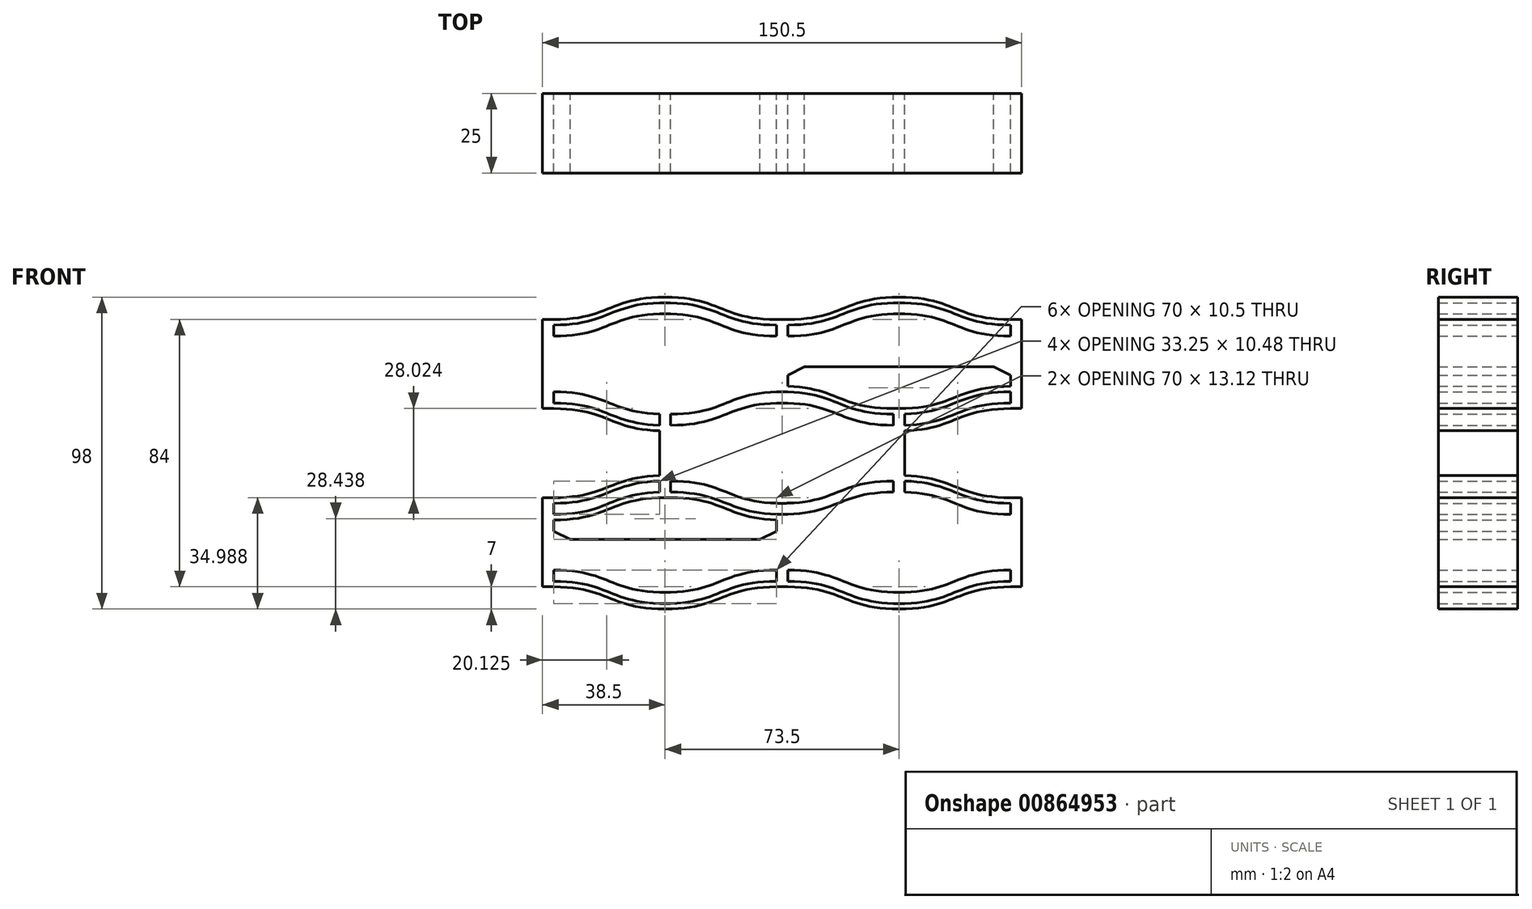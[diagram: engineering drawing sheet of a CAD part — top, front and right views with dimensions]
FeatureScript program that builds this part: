
annotation { "Feature Type Name" : "Feature", "Feature Type Description" : "" }
export const myFeature = defineFeature(function(context is Context, id is Id, definition is map)
    precondition{}
    {
        {
            var Q0;
            Q0=qCreatedBy(makeId("Front.planeOp"),FACE);
            var sketch = newSketch(context, id + "F0", { "sketchPlane" : qUnion([Q0])});
            skPoint(sketch, "E0", {"position": v(0, 0) * mm});
            skFitSpline(sketch, "E1", {"points": [v(38.5, -7) * mm, v(56, -3.5) * mm, v(73.5, 0) * mm], "startDerivative": vector(52.5, 0) * mm, "endDerivative": vector(52.5, 0) * mm});
            skFitSpline(sketch, "E2", {"points": [v(73.5, 7) * mm, v(56, 3.5) * mm, v(38.5, 0) * mm], "startDerivative": vector(-52.5, 0) * mm, "endDerivative": vector(-52.5, 0) * mm});
            skFitSpline(sketch, "E3", {"points": [v(73.5, 5.25) * mm, v(56, 1.75) * mm, v(38.5, -1.75) * mm], "startDerivative": vector(-52.5, 0) * mm, "endDerivative": vector(-52.5, 0) * mm});
            skFitSpline(sketch, "E4", {"points": [v(73.5, 1.75) * mm, v(56, -1.75) * mm, v(38.5, -5.25) * mm], "startDerivative": vector(-52.5, 0) * mm, "endDerivative": vector(-52.5, 0) * mm});
            skLineSegment(sketch, "E5", {"start": v(73.5, 26.25) * mm, "end": v(73.5, 22.75) * mm});
            skLineSegment(sketch, "E6", {"start": v(70, 0) * mm, "end": v(73.5, 0) * mm});
            skLineSegment(sketch, "E7.trimOffspring", {"start": v(73.5, 5.25) * mm, "end": v(73.5, 1.75) * mm});
            skLineSegment(sketch, "E8.trimOffspring", {"start": v(73.5, 10.5) * mm, "end": v(73.5, 7) * mm});
            skLineSegment(sketch, "E9.trimOffspring", {"start": v(73.5, 21) * mm, "end": v(73.5, 17.5) * mm});
            skLineSegment(sketch, "E10", {"start": v(73.5, 1.75) * mm, "end": v(73.5, 5.25) * mm});
            skLineSegment(sketch, "E11", {"start": v(3.5, 26.25) * mm, "end": v(3.5, 22.75) * mm});
            skLineSegment(sketch, "E12", {"start": v(68.25, 13.13) * mm, "end": v(8.75, 13.13) * mm});
            skLineSegment(sketch, "E13", {"start": v(68.25, 14.88) * mm, "end": v(8.75, 14.88) * mm});
            skLineSegment(sketch, "E14", {"start": v(3.5, 28) * mm, "end": v(0, 28) * mm});
            skLineSegment(sketch, "E15", {"start": v(73.5, 17.5) * mm, "end": v(68.25, 14.87) * mm});
            skLineSegment(sketch, "E16", {"start": v(68.25, 13.13) * mm, "end": v(73.5, 10.5) * mm});
            skLineSegment(sketch, "E17", {"start": v(3.5, 10.5) * mm, "end": v(8.75, 13.12) * mm});
            skLineSegment(sketch, "E18", {"start": v(3.5, 17.5) * mm, "end": v(8.75, 14.87) * mm});
            skFitSpline(sketch, "E19", {"points": [v(73.5, 21) * mm, v(56, 24.5) * mm, v(38.5, 28) * mm], "startDerivative": vector(-52.5, 0) * mm, "endDerivative": vector(-52.5, 0) * mm});
            skFitSpline(sketch, "E20", {"points": [v(73.5, 22.75) * mm, v(56, 26.25) * mm, v(38.5, 29.75) * mm], "startDerivative": vector(-52.5, 0) * mm, "endDerivative": vector(-52.5, 0) * mm});
            skFitSpline(sketch, "E21", {"points": [v(73.5, 26.25) * mm, v(56, 29.75) * mm, v(38.5, 33.25) * mm], "startDerivative": vector(-52.5, 0) * mm, "endDerivative": vector(-52.5, 0) * mm});
            skFitSpline(sketch, "E22", {"points": [v(73.5, 28) * mm, v(56, 31.5) * mm, v(38.5, 35) * mm], "startDerivative": vector(-52.5, 0) * mm, "endDerivative": vector(-52.5, 0) * mm});
            skFitSpline(sketch, "E23", {"points": [v(3.5, 1.75) * mm, v(21, -1.75) * mm, v(38.5, -5.25) * mm], "startDerivative": vector(52.5, 0) * mm, "endDerivative": vector(52.5, 0) * mm});
            skFitSpline(sketch, "E24", {"points": [v(3.5, 0) * mm, v(21, -3.5) * mm, v(38.5, -7) * mm], "startDerivative": vector(52.5, 0) * mm, "endDerivative": vector(52.5, 0) * mm});
            skFitSpline(sketch, "E25", {"points": [v(38.5, -1.75) * mm, v(21, 1.75) * mm, v(3.5, 5.25) * mm], "startDerivative": vector(-52.5, 0) * mm, "endDerivative": vector(-52.5, 0) * mm});
            skFitSpline(sketch, "E26", {"points": [v(38.5, 0) * mm, v(21, 3.5) * mm, v(3.5, 6.97) * mm], "startDerivative": vector(-52.5, 0) * mm, "endDerivative": vector(-52.5, 0) * mm});
            skFitSpline(sketch, "E27", {"points": [v(73.5, 7) * mm, v(56, 3.5) * mm, v(38.5, 0) * mm], "startDerivative": vector(-52.5, 0) * mm, "endDerivative": vector(-52.5, 0) * mm});
            skFitSpline(sketch, "E28", {"points": [v(38.5, 35) * mm, v(21, 31.5) * mm, v(3.5, 28) * mm], "startDerivative": vector(-52.5, 0) * mm, "endDerivative": vector(-52.5, 0) * mm});
            skFitSpline(sketch, "E29", {"points": [v(38.5, 33.25) * mm, v(21, 29.75) * mm, v(3.5, 26.25) * mm], "startDerivative": vector(-52.5, 0) * mm, "endDerivative": vector(-52.5, 0) * mm});
            skFitSpline(sketch, "E30", {"points": [v(38.5, 29.75) * mm, v(21, 26.25) * mm, v(3.5, 22.75) * mm], "startDerivative": vector(-52.5, 0) * mm, "endDerivative": vector(-52.5, 0) * mm});
            skFitSpline(sketch, "E31", {"points": [v(38.5, 27.97) * mm, v(21, 24.47) * mm, v(3.5, 20.97) * mm], "startDerivative": vector(-52.5, 0) * mm, "endDerivative": vector(-52.5, 0) * mm});
            skFitSpline(sketch, "E32", {"points": [v(38.5, -7) * mm, v(56, -3.5) * mm, v(73.5, 0) * mm], "startDerivative": vector(52.5, 0) * mm, "endDerivative": vector(52.5, 0) * mm});
            skFitSpline(sketch, "E33", {"points": [v(38.5, -5.25) * mm, v(56, -1.75) * mm, v(73.5, 1.75) * mm], "startDerivative": vector(52.5, 0) * mm, "endDerivative": vector(52.5, 0) * mm});
            skFitSpline(sketch, "E34", {"points": [v(38.5, -1.75) * mm, v(56, 1.75) * mm, v(73.5, 5.25) * mm], "startDerivative": vector(52.5, 0) * mm, "endDerivative": vector(52.5, 0) * mm});
            skLineSegment(sketch, "E35", {"start": v(40.25, -3.53) * mm, "end": v(40.25, -5.23) * mm});
            skLineSegment(sketch, "E36", {"start": v(40.25, -5.23) * mm, "end": v(40.25, -1.73) * mm});
            skLineSegment(sketch, "E37", {"start": v(36.75, -3.53) * mm, "end": v(36.75, -5.23) * mm});
            skLineSegment(sketch, "E38", {"start": v(36.75, -5.23) * mm, "end": v(36.75, -1.73) * mm});
            skLineSegment(sketch, "E39", {"start": v(40.25, 31.53) * mm, "end": v(40.25, 29.73) * mm});
            skLineSegment(sketch, "E40", {"start": v(40.25, 29.73) * mm, "end": v(40.25, 33.23) * mm});
            skLineSegment(sketch, "E41", {"start": v(36.75, 29.73) * mm, "end": v(36.75, 33.23) * mm});
            skLineSegment(sketch, "E42.trimOffspring", {"start": v(73.5, 22.75) * mm, "end": v(73.5, 26.25) * mm});
            skLineSegment(sketch, "E43.trimOffspring", {"start": v(73.5, 17.5) * mm, "end": v(73.5, 21) * mm});
            skLineSegment(sketch, "E44.trimOffspring", {"start": v(73.5, 7) * mm, "end": v(73.5, 10.5) * mm});
            skLineSegment(sketch, "E45.trimOffspring", {"start": v(3.5, 21) * mm, "end": v(3.5, 17.5) * mm});
            skLineSegment(sketch, "E46.trimOffspring", {"start": v(3.5, 10.5) * mm, "end": v(3.5, 7) * mm});
            skLineSegment(sketch, "E47.trimOffspring", {"start": v(3.5, 5.25) * mm, "end": v(3.5, 1.75) * mm});
            skLineSegment(sketch, "E48.left", {"start": v(0, 26.27) * mm, "end": v(0, 22.77) * mm});
            skPoint(sketch, "E49", {"position": v(77, 28) * mm});
            skLineSegment(sketch, "E50", {"start": v(75.25, 28) * mm, "end": v(76.25, 28) * mm});
            skLineSegment(sketch, "E51", {"start": v(77, 1.73) * mm, "end": v(77, 21.02) * mm});
            skLineSegment(sketch, "E52", {"start": v(73.5, 0) * mm, "end": v(77, 0) * mm});
            skPoint(sketch, "E53", {"position": v(36.75, 28) * mm});
            skLineSegment(sketch, "E54", {"start": v(76.25, 28) * mm, "end": v(75.25, 28) * mm});
            skLineSegment(sketch, "E55", {"start": v(71.75, 28) * mm, "end": v(75.25, 28) * mm});
            skFitSpline(sketch, "E56", {"points": [v(75.25, 21) * mm, v(92.75, 24.5) * mm, v(110.25, 28) * mm], "startDerivative": vector(52.5, 0) * mm, "endDerivative": vector(52.5, 0) * mm});
            skFitSpline(sketch, "E57", {"points": [v(110.25, 35) * mm, v(92.75, 31.5) * mm, v(75.25, 28) * mm], "startDerivative": vector(-52.5, 0) * mm, "endDerivative": vector(-52.5, 0) * mm});
            skFitSpline(sketch, "E58", {"points": [v(110.25, 33.25) * mm, v(92.75, 29.75) * mm, v(75.25, 26.25) * mm], "startDerivative": vector(-52.5, 0) * mm, "endDerivative": vector(-52.5, 0) * mm});
            skFitSpline(sketch, "E59", {"points": [v(110.25, 29.75) * mm, v(92.75, 26.25) * mm, v(75.25, 22.75) * mm], "startDerivative": vector(-52.5, 0) * mm, "endDerivative": vector(-52.5, 0) * mm});
            skLineSegment(sketch, "E60", {"start": v(110.25, 56) * mm, "end": v(106.75, 56) * mm});
            skLineSegment(sketch, "E61", {"start": v(106.75, 56) * mm, "end": v(110.25, 56) * mm});
            skLineSegment(sketch, "E62", {"start": v(110.25, 54.25) * mm, "end": v(110.25, 50.75) * mm});
            skLineSegment(sketch, "E63", {"start": v(106.75, 28) * mm, "end": v(110.25, 28) * mm});
            skLineSegment(sketch, "E64.trimOffspring", {"start": v(110.25, 33.25) * mm, "end": v(110.25, 29.75) * mm});
            skLineSegment(sketch, "E65.trimOffspring", {"start": v(110.25, 38.5) * mm, "end": v(110.25, 35) * mm});
            skLineSegment(sketch, "E66.trimOffspring", {"start": v(110.25, 49) * mm, "end": v(110.25, 45.5) * mm});
            skLineSegment(sketch, "E67", {"start": v(110.25, 29.75) * mm, "end": v(110.25, 33.25) * mm});
            skLineSegment(sketch, "E68", {"start": v(36.75, 29.73) * mm, "end": v(36.75, 33.25) * mm});
            skLineSegment(sketch, "E69", {"start": v(40.25, 54.25) * mm, "end": v(40.25, 50.75) * mm});
            skLineSegment(sketch, "E70", {"start": v(105, 41.12) * mm, "end": v(45.5, 41.13) * mm});
            skLineSegment(sketch, "E71", {"start": v(105, 42.87) * mm, "end": v(45.5, 42.88) * mm});
            skLineSegment(sketch, "E72", {"start": v(110.25, 45.5) * mm, "end": v(105, 42.87) * mm});
            skLineSegment(sketch, "E73", {"start": v(105, 41.13) * mm, "end": v(110.25, 38.5) * mm});
            skLineSegment(sketch, "E74", {"start": v(40.25, 38.5) * mm, "end": v(45.5, 41.12) * mm});
            skLineSegment(sketch, "E75", {"start": v(40.25, 45.5) * mm, "end": v(45.5, 42.88) * mm});
            skFitSpline(sketch, "E76", {"points": [v(110.25, 49) * mm, v(92.75, 52.5) * mm, v(75.25, 56) * mm], "startDerivative": vector(-52.5, 0) * mm, "endDerivative": vector(-52.5, 0) * mm});
            skFitSpline(sketch, "E77", {"points": [v(110.25, 50.75) * mm, v(92.75, 54.25) * mm, v(75.25, 57.75) * mm], "startDerivative": vector(-52.5, 0) * mm, "endDerivative": vector(-52.5, 0) * mm});
            skFitSpline(sketch, "E78", {"points": [v(110.25, 54.25) * mm, v(92.75, 57.75) * mm, v(75.25, 61.25) * mm], "startDerivative": vector(-52.5, 0) * mm, "endDerivative": vector(-52.5, 0) * mm});
            skFitSpline(sketch, "E79", {"points": [v(110.25, 56) * mm, v(92.75, 59.5) * mm, v(75.25, 63) * mm], "startDerivative": vector(-52.5, 0) * mm, "endDerivative": vector(-52.5, 0) * mm});
            skFitSpline(sketch, "E80", {"points": [v(110.25, 35) * mm, v(92.75, 31.5) * mm, v(75.25, 28) * mm], "startDerivative": vector(-52.5, 0) * mm, "endDerivative": vector(-52.5, 0) * mm});
            skFitSpline(sketch, "E81", {"points": [v(75.25, 63) * mm, v(57.75, 59.5) * mm, v(40.25, 56) * mm], "startDerivative": vector(-52.5, 0) * mm, "endDerivative": vector(-52.5, 0) * mm});
            skFitSpline(sketch, "E82", {"points": [v(75.25, 61.25) * mm, v(57.75, 57.75) * mm, v(40.25, 54.25) * mm], "startDerivative": vector(-52.5, 0) * mm, "endDerivative": vector(-52.5, 0) * mm});
            skFitSpline(sketch, "E83", {"points": [v(75.25, 57.75) * mm, v(57.75, 54.25) * mm, v(40.25, 50.75) * mm], "startDerivative": vector(-52.5, 0) * mm, "endDerivative": vector(-52.5, 0) * mm});
            skFitSpline(sketch, "E84", {"points": [v(75.25, 55.97) * mm, v(57.75, 52.47) * mm, v(40.25, 48.97) * mm], "startDerivative": vector(-52.5, 0) * mm, "endDerivative": vector(-52.5, 0) * mm});
            skFitSpline(sketch, "E85", {"points": [v(75.25, 21) * mm, v(92.75, 24.5) * mm, v(110.25, 28) * mm], "startDerivative": vector(52.5, 0) * mm, "endDerivative": vector(52.5, 0) * mm});
            skFitSpline(sketch, "E86", {"points": [v(75.25, 22.75) * mm, v(92.75, 26.25) * mm, v(110.25, 29.75) * mm], "startDerivative": vector(52.5, 0) * mm, "endDerivative": vector(52.5, 0) * mm});
            skFitSpline(sketch, "E87", {"points": [v(75.25, 26.25) * mm, v(92.75, 29.75) * mm, v(110.25, 33.25) * mm], "startDerivative": vector(52.5, 0) * mm, "endDerivative": vector(52.5, 0) * mm});
            skLineSegment(sketch, "E88", {"start": v(77, 24.47) * mm, "end": v(77, 22.77) * mm});
            skLineSegment(sketch, "E89", {"start": v(77, 22.77) * mm, "end": v(77, 26.27) * mm});
            skLineSegment(sketch, "E90", {"start": v(73.5, 24.47) * mm, "end": v(73.5, 22.77) * mm});
            skLineSegment(sketch, "E91", {"start": v(73.5, 22.77) * mm, "end": v(73.5, 26.27) * mm});
            skLineSegment(sketch, "E92", {"start": v(77, 59.53) * mm, "end": v(77, 57.73) * mm});
            skLineSegment(sketch, "E93", {"start": v(77, 57.73) * mm, "end": v(77, 61.23) * mm});
            skLineSegment(sketch, "E94", {"start": v(73.5, 57.73) * mm, "end": v(73.5, 61.23) * mm});
            skLineSegment(sketch, "E95.trimOffspring", {"start": v(110.25, 50.75) * mm, "end": v(110.25, 54.25) * mm});
            skLineSegment(sketch, "E96.trimOffspring", {"start": v(110.25, 45.5) * mm, "end": v(110.25, 49) * mm});
            skLineSegment(sketch, "E97.trimOffspring", {"start": v(110.25, 35) * mm, "end": v(110.25, 38.5) * mm});
            skLineSegment(sketch, "E98.trimOffspring", {"start": v(40.25, 49) * mm, "end": v(40.25, 45.5) * mm});
            skLineSegment(sketch, "E99.trimOffspring", {"start": v(40.25, 38.5) * mm, "end": v(40.25, 35) * mm});
            skLineSegment(sketch, "E100.trimOffspring", {"start": v(40.25, 33.25) * mm, "end": v(40.25, 29.75) * mm});
            skLineSegment(sketch, "E101.left", {"start": v(36.75, 54.25) * mm, "end": v(36.75, 50.75) * mm});
            skPoint(sketch, "E102", {"position": v(113.75, 56) * mm});
            skPoint(sketch, "E103", {"position": v(113.75, 28) * mm});
            skLineSegment(sketch, "E104", {"start": v(110.25, 56) * mm, "end": v(113.75, 56) * mm});
            skLineSegment(sketch, "E105", {"start": v(113.75, 28) * mm, "end": v(113.75, 56) * mm});
            skLineSegment(sketch, "E106", {"start": v(110.25, 28) * mm, "end": v(113.75, 28) * mm});
            skPoint(sketch, "E107", {"position": v(73.5, 56) * mm});
            skPoint(sketch, "E108.endDerivative.orphan", {"position": v(66.5, 21) * mm});
            skPoint(sketch, "E109.startDerivative.orphan", {"position": v(49, 29.75) * mm});
            skPoint(sketch, "E110.startDerivative.orphan", {"position": v(66.5, 26.25) * mm});
            skPoint(sketch, "E111.end.orphan", {"position": v(40.26, 34.97) * mm});
            skPoint(sketch, "E111.endDerivative.orphan", {"position": v(49, 34.97) * mm});
            skPoint(sketch, "E112", {"position": v(40.25, 0) * mm});
            skPoint(sketch, "E113", {"position": v(43.2, -30) * mm});
            skLineSegment(sketch, "E114", {"start": v(0.75, 0) * mm, "end": v(1.75, 0) * mm});
            skLineSegment(sketch, "E115", {"start": v(5.25, 0) * mm, "end": v(1.75, 0) * mm});
            skFitSpline(sketch, "E116", {"points": [v(1.75, 7) * mm, v(-15.75, 3.5) * mm, v(-33.25, 0) * mm], "startDerivative": vector(-52.5, 0) * mm, "endDerivative": vector(-52.5, 0) * mm});
            skFitSpline(sketch, "E117", {"points": [v(-33.25, -7) * mm, v(-15.75, -3.5) * mm, v(1.75, 0) * mm], "startDerivative": vector(52.5, 0) * mm, "endDerivative": vector(52.5, 0) * mm});
            skFitSpline(sketch, "E118", {"points": [v(-33.25, -5.25) * mm, v(-15.75, -1.75) * mm, v(1.75, 1.75) * mm], "startDerivative": vector(52.5, 0) * mm, "endDerivative": vector(52.5, 0) * mm});
            skFitSpline(sketch, "E119", {"points": [v(-33.25, -1.75) * mm, v(-15.75, 1.75) * mm, v(1.75, 5.25) * mm], "startDerivative": vector(52.5, 0) * mm, "endDerivative": vector(52.5, 0) * mm});
            skLineSegment(sketch, "E120", {"start": v(-33.25, -28) * mm, "end": v(-29.75, -28) * mm});
            skLineSegment(sketch, "E121", {"start": v(-29.75, -28) * mm, "end": v(-33.25, -28) * mm});
            skLineSegment(sketch, "E122", {"start": v(-33.25, -26.25) * mm, "end": v(-33.25, -22.75) * mm});
            skLineSegment(sketch, "E123", {"start": v(-29.75, 0) * mm, "end": v(-33.25, 0) * mm});
            skLineSegment(sketch, "E124.trimOffspring", {"start": v(-33.25, -5.25) * mm, "end": v(-33.25, -1.75) * mm});
            skLineSegment(sketch, "E125.trimOffspring", {"start": v(-33.25, -10.5) * mm, "end": v(-33.25, -7) * mm});
            skLineSegment(sketch, "E126.trimOffspring", {"start": v(-33.25, -21) * mm, "end": v(-33.25, -17.5) * mm});
            skLineSegment(sketch, "E127", {"start": v(-33.25, -1.75) * mm, "end": v(-33.25, -5.25) * mm});
            skLineSegment(sketch, "E128", {"start": v(40.25, -1.73) * mm, "end": v(40.25, -5.25) * mm});
            skLineSegment(sketch, "E129", {"start": v(36.75, -26.25) * mm, "end": v(36.75, -22.75) * mm});
            skLineSegment(sketch, "E130", {"start": v(-28, -13.12) * mm, "end": v(31.5, -13.13) * mm});
            skLineSegment(sketch, "E131", {"start": v(-28, -14.87) * mm, "end": v(31.5, -14.87) * mm});
            skLineSegment(sketch, "E132", {"start": v(36.75, -28) * mm, "end": v(40.25, -28) * mm});
            skLineSegment(sketch, "E133", {"start": v(-33.25, -17.5) * mm, "end": v(-28, -14.87) * mm});
            skLineSegment(sketch, "E134", {"start": v(-28, -13.13) * mm, "end": v(-33.25, -10.5) * mm});
            skLineSegment(sketch, "E135", {"start": v(36.75, -10.5) * mm, "end": v(31.5, -13.12) * mm});
            skLineSegment(sketch, "E136", {"start": v(36.75, -17.5) * mm, "end": v(31.5, -14.87) * mm});
            skFitSpline(sketch, "E137", {"points": [v(-33.25, -21) * mm, v(-15.75, -24.5) * mm, v(1.75, -28) * mm], "startDerivative": vector(52.5, 0) * mm, "endDerivative": vector(52.5, 0) * mm});
            skFitSpline(sketch, "E138", {"points": [v(-33.25, -22.75) * mm, v(-15.75, -26.25) * mm, v(1.75, -29.75) * mm], "startDerivative": vector(52.5, 0) * mm, "endDerivative": vector(52.5, 0) * mm});
            skFitSpline(sketch, "E139", {"points": [v(-33.25, -26.25) * mm, v(-15.75, -29.75) * mm, v(1.75, -33.25) * mm], "startDerivative": vector(52.5, 0) * mm, "endDerivative": vector(52.5, 0) * mm});
            skFitSpline(sketch, "E140", {"points": [v(-33.25, -28) * mm, v(-15.75, -31.5) * mm, v(1.75, -35) * mm], "startDerivative": vector(52.5, 0) * mm, "endDerivative": vector(52.5, 0) * mm});
            skFitSpline(sketch, "E141", {"points": [v(-33.25, -7) * mm, v(-15.75, -3.5) * mm, v(1.75, 0) * mm], "startDerivative": vector(52.5, 0) * mm, "endDerivative": vector(52.5, 0) * mm});
            skFitSpline(sketch, "E142", {"points": [v(1.75, -35) * mm, v(19.25, -31.5) * mm, v(36.75, -28) * mm], "startDerivative": vector(52.5, 0) * mm, "endDerivative": vector(52.5, 0) * mm});
            skFitSpline(sketch, "E143", {"points": [v(1.75, -33.25) * mm, v(19.25, -29.75) * mm, v(36.75, -26.25) * mm], "startDerivative": vector(52.5, 0) * mm, "endDerivative": vector(52.5, 0) * mm});
            skFitSpline(sketch, "E144", {"points": [v(1.75, -29.75) * mm, v(19.25, -26.25) * mm, v(36.75, -22.75) * mm], "startDerivative": vector(52.5, 0) * mm, "endDerivative": vector(52.5, 0) * mm});
            skFitSpline(sketch, "E145", {"points": [v(1.75, -27.97) * mm, v(19.25, -24.47) * mm, v(36.75, -20.97) * mm], "startDerivative": vector(52.5, 0) * mm, "endDerivative": vector(52.5, 0) * mm});
            skFitSpline(sketch, "E146", {"points": [v(1.75, 7) * mm, v(-15.75, 3.5) * mm, v(-33.25, 0) * mm], "startDerivative": vector(-52.5, 0) * mm, "endDerivative": vector(-52.5, 0) * mm});
            skFitSpline(sketch, "E147", {"points": [v(1.75, 5.25) * mm, v(-15.75, 1.75) * mm, v(-33.25, -1.75) * mm], "startDerivative": vector(-52.5, 0) * mm, "endDerivative": vector(-52.5, 0) * mm});
            skFitSpline(sketch, "E148", {"points": [v(1.75, 1.75) * mm, v(-15.75, -1.75) * mm, v(-33.25, -5.25) * mm], "startDerivative": vector(-52.5, 0) * mm, "endDerivative": vector(-52.5, 0) * mm});
            skLineSegment(sketch, "E149", {"start": v(0, 3.53) * mm, "end": v(0, 5.23) * mm});
            skLineSegment(sketch, "E150", {"start": v(0, 5.23) * mm, "end": v(0, 1.73) * mm});
            skLineSegment(sketch, "E151", {"start": v(3.5, 3.53) * mm, "end": v(3.5, 5.23) * mm});
            skLineSegment(sketch, "E152", {"start": v(3.5, 5.23) * mm, "end": v(3.5, 1.73) * mm});
            skLineSegment(sketch, "E153", {"start": v(0, -31.53) * mm, "end": v(0, -29.73) * mm});
            skLineSegment(sketch, "E154", {"start": v(0, -29.73) * mm, "end": v(0, -33.23) * mm});
            skLineSegment(sketch, "E155", {"start": v(3.5, -29.73) * mm, "end": v(3.5, -33.23) * mm});
            skLineSegment(sketch, "E156.trimOffspring", {"start": v(-33.25, -22.75) * mm, "end": v(-33.25, -26.25) * mm});
            skLineSegment(sketch, "E157.trimOffspring", {"start": v(-33.25, -17.5) * mm, "end": v(-33.25, -21) * mm});
            skLineSegment(sketch, "E158.trimOffspring", {"start": v(-33.25, -7) * mm, "end": v(-33.25, -10.5) * mm});
            skLineSegment(sketch, "E159.trimOffspring", {"start": v(36.75, -21) * mm, "end": v(36.75, -17.5) * mm});
            skLineSegment(sketch, "E160.trimOffspring", {"start": v(36.75, -10.5) * mm, "end": v(36.75, -7) * mm});
            skLineSegment(sketch, "E161.trimOffspring", {"start": v(36.75, -5.25) * mm, "end": v(36.75, -1.75) * mm});
            skLineSegment(sketch, "E162.left", {"start": v(40.25, -26.25) * mm, "end": v(40.25, -22.75) * mm});
            skPoint(sketch, "E163", {"position": v(-36.75, -28) * mm});
            skPoint(sketch, "E164", {"position": v(-36.75, 0) * mm});
            skLineSegment(sketch, "E165", {"start": v(-33.25, -28) * mm, "end": v(-36.75, -28) * mm});
            skLineSegment(sketch, "E166", {"start": v(-36.75, 0) * mm, "end": v(-36.75, -28) * mm});
            skLineSegment(sketch, "E167", {"start": v(-33.25, 0) * mm, "end": v(-36.75, 0) * mm});
            skPoint(sketch, "E168", {"position": v(3.5, -28) * mm});
            skPoint(sketch, "E169.endDerivative.orphan", {"position": v(10.5, 7) * mm});
            skPoint(sketch, "E170.startDerivative.orphan", {"position": v(28, -1.75) * mm});
            skPoint(sketch, "E171.startDerivative.orphan", {"position": v(10.5, 1.75) * mm});
            skPoint(sketch, "E172.end.orphan", {"position": v(36.74, -6.97) * mm});
            skPoint(sketch, "E172.endDerivative.orphan", {"position": v(28, -6.97) * mm});
            skPoint(sketch, "E173", {"position": v(-36.75, 28) * mm});
            skLineSegment(sketch, "E174", {"start": v(1.75, 28) * mm, "end": v(0, 28) * mm});
            skLineSegment(sketch, "E175", {"start": v(0, 28) * mm, "end": v(1.75, 28) * mm});
            skLineSegment(sketch, "E176.trimOffspring", {"start": v(36.75, 33.25) * mm, "end": v(36.75, 29.75) * mm});
            skLineSegment(sketch, "E177.trimOffspring", {"start": v(36.75, 38.5) * mm, "end": v(36.75, 35) * mm});
            skLineSegment(sketch, "E178.trimOffspring", {"start": v(36.75, 49) * mm, "end": v(36.75, 45.5) * mm});
            skLineSegment(sketch, "E179", {"start": v(36.75, 29.75) * mm, "end": v(36.75, 33.25) * mm});
            skLineSegment(sketch, "E180", {"start": v(-36.75, 28) * mm, "end": v(-36.75, 56) * mm});
            skLineSegment(sketch, "E181", {"start": v(-33.25, 54.25) * mm, "end": v(-33.25, 50.75) * mm});
            skLineSegment(sketch, "E182", {"start": v(31.5, 41.13) * mm, "end": v(-28, 41.13) * mm});
            skLineSegment(sketch, "E183", {"start": v(31.5, 42.88) * mm, "end": v(-28, 42.88) * mm});
            skLineSegment(sketch, "E184", {"start": v(-33.25, 28) * mm, "end": v(-36.75, 28) * mm});
            skLineSegment(sketch, "E185", {"start": v(-33.25, 56) * mm, "end": v(-36.75, 56) * mm});
            skLineSegment(sketch, "E186", {"start": v(36.75, 45.5) * mm, "end": v(31.5, 42.88) * mm});
            skLineSegment(sketch, "E187", {"start": v(31.5, 41.13) * mm, "end": v(36.75, 38.5) * mm});
            skLineSegment(sketch, "E188", {"start": v(-33.25, 38.5) * mm, "end": v(-28, 41.13) * mm});
            skLineSegment(sketch, "E189", {"start": v(-33.25, 45.5) * mm, "end": v(-28, 42.88) * mm});
            skFitSpline(sketch, "E190", {"points": [v(36.75, 49) * mm, v(19.25, 52.5) * mm, v(1.75, 56) * mm], "startDerivative": vector(-52.5, 0) * mm, "endDerivative": vector(-52.5, 0) * mm});
            skFitSpline(sketch, "E191", {"points": [v(36.75, 50.75) * mm, v(19.25, 54.25) * mm, v(1.75, 57.75) * mm], "startDerivative": vector(-52.5, 0) * mm, "endDerivative": vector(-52.5, 0) * mm});
            skFitSpline(sketch, "E192", {"points": [v(36.75, 54.25) * mm, v(19.25, 57.75) * mm, v(1.75, 61.25) * mm], "startDerivative": vector(-52.5, 0) * mm, "endDerivative": vector(-52.5, 0) * mm});
            skFitSpline(sketch, "E193", {"points": [v(36.75, 56) * mm, v(19.25, 59.5) * mm, v(1.75, 63) * mm], "startDerivative": vector(-52.5, 0) * mm, "endDerivative": vector(-52.5, 0) * mm});
            skFitSpline(sketch, "E194", {"points": [v(-33.25, 29.75) * mm, v(-15.75, 26.25) * mm, v(1.75, 22.75) * mm], "startDerivative": vector(52.5, 0) * mm, "endDerivative": vector(52.5, 0) * mm});
            skFitSpline(sketch, "E195", {"points": [v(-33.25, 28) * mm, v(-15.75, 24.5) * mm, v(1.75, 21) * mm], "startDerivative": vector(52.5, 0) * mm, "endDerivative": vector(52.5, 0) * mm});
            skFitSpline(sketch, "E196", {"points": [v(1.75, 26.25) * mm, v(-15.75, 29.75) * mm, v(-33.25, 33.25) * mm], "startDerivative": vector(-52.5, 0) * mm, "endDerivative": vector(-52.5, 0) * mm});
            skFitSpline(sketch, "E197", {"points": [v(1.75, 28) * mm, v(-15.75, 31.5) * mm, v(-33.24, 34.97) * mm], "startDerivative": vector(-52.5, 0) * mm, "endDerivative": vector(-52.5, 0) * mm});
            skFitSpline(sketch, "E198", {"points": [v(1.75, 63) * mm, v(-15.75, 59.5) * mm, v(-33.25, 56) * mm], "startDerivative": vector(-52.5, 0) * mm, "endDerivative": vector(-52.5, 0) * mm});
            skFitSpline(sketch, "E199", {"points": [v(1.75, 61.25) * mm, v(-15.75, 57.75) * mm, v(-33.25, 54.25) * mm], "startDerivative": vector(-52.5, 0) * mm, "endDerivative": vector(-52.5, 0) * mm});
            skFitSpline(sketch, "E200", {"points": [v(1.75, 57.75) * mm, v(-15.75, 54.25) * mm, v(-33.25, 50.75) * mm], "startDerivative": vector(-52.5, 0) * mm, "endDerivative": vector(-52.5, 0) * mm});
            skFitSpline(sketch, "E201", {"points": [v(1.75, 55.97) * mm, v(-15.75, 52.47) * mm, v(-33.25, 48.97) * mm], "startDerivative": vector(-52.5, 0) * mm, "endDerivative": vector(-52.5, 0) * mm});
            skLineSegment(sketch, "E202", {"start": v(3.5, 24.47) * mm, "end": v(3.5, 22.77) * mm});
            skLineSegment(sketch, "E203", {"start": v(3.5, 22.77) * mm, "end": v(3.5, 26.27) * mm});
            skLineSegment(sketch, "E204", {"start": v(0, 24.47) * mm, "end": v(0, 22.77) * mm});
            skLineSegment(sketch, "E205", {"start": v(0, 22.77) * mm, "end": v(0, 26.27) * mm});
            skLineSegment(sketch, "E206", {"start": v(3.5, 59.53) * mm, "end": v(3.5, 57.73) * mm});
            skLineSegment(sketch, "E207", {"start": v(3.5, 57.73) * mm, "end": v(3.5, 61.23) * mm});
            skLineSegment(sketch, "E208", {"start": v(0, 57.73) * mm, "end": v(0, 61.23) * mm});
            skLineSegment(sketch, "E209.trimOffspring", {"start": v(36.75, 50.75) * mm, "end": v(36.75, 54.25) * mm});
            skLineSegment(sketch, "E210.trimOffspring", {"start": v(36.75, 45.5) * mm, "end": v(36.75, 49) * mm});
            skLineSegment(sketch, "E211.trimOffspring", {"start": v(36.75, 35) * mm, "end": v(36.75, 38.5) * mm});
            skLineSegment(sketch, "E212.trimOffspring", {"start": v(-33.25, 49) * mm, "end": v(-33.25, 45.5) * mm});
            skLineSegment(sketch, "E213.trimOffspring", {"start": v(-33.25, 38.5) * mm, "end": v(-33.25, 35) * mm});
            skLineSegment(sketch, "E214.trimOffspring", {"start": v(-33.25, 33.25) * mm, "end": v(-33.25, 29.75) * mm});
            skLineSegment(sketch, "E215.left", {"start": v(-36.75, 56) * mm, "end": v(-36.75, 28) * mm});
            skPoint(sketch, "E216", {"position": v(40.25, 28) * mm});
            skLineSegment(sketch, "E217", {"start": v(36.75, 56) * mm, "end": v(40.25, 56) * mm});
            skLineSegment(sketch, "E218", {"start": v(40.25, 29.75) * mm, "end": v(40.25, 33.25) * mm});
            skLineSegment(sketch, "E219", {"start": v(36.75, 28) * mm, "end": v(40.25, 28) * mm});
            skPoint(sketch, "E220.startDerivative.orphan", {"position": v(10.5, 21) * mm});
            skPoint(sketch, "E221.start.orphan", {"position": v(36.75, 33.25) * mm});
            skPoint(sketch, "E221.startDerivative.orphan", {"position": v(28, 33.25) * mm});
            skPoint(sketch, "E222.start.orphan", {"position": v(36.75, 35) * mm});
            skPoint(sketch, "E222.startDerivative.orphan", {"position": v(28, 35) * mm});
            skPoint(sketch, "E223.start.orphan", {"position": v(36.75, 29.75) * mm});
            skPoint(sketch, "E223.startDerivative.orphan", {"position": v(28, 29.75) * mm});
            skPoint(sketch, "E224", {"position": v(113.75, 0) * mm});
            skLineSegment(sketch, "E225", {"start": v(75.25, 0) * mm, "end": v(78.75, 0) * mm});
            skLineSegment(sketch, "E226", {"start": v(78.75, 0) * mm, "end": v(75.25, 0) * mm});
            skLineSegment(sketch, "E227.trimOffspring", {"start": v(40.25, -5.25) * mm, "end": v(40.25, -1.75) * mm});
            skLineSegment(sketch, "E228.trimOffspring", {"start": v(40.25, -10.5) * mm, "end": v(40.25, -7) * mm});
            skLineSegment(sketch, "E229.trimOffspring", {"start": v(40.25, -21) * mm, "end": v(40.25, -17.5) * mm});
            skLineSegment(sketch, "E230", {"start": v(40.25, -1.75) * mm, "end": v(40.25, -5.25) * mm});
            skLineSegment(sketch, "E231", {"start": v(113.75, 0) * mm, "end": v(113.75, -28) * mm});
            skLineSegment(sketch, "E232", {"start": v(110.25, -26.25) * mm, "end": v(110.25, -22.75) * mm});
            skLineSegment(sketch, "E233", {"start": v(45.5, -13.13) * mm, "end": v(105, -13.13) * mm});
            skLineSegment(sketch, "E234", {"start": v(45.5, -14.88) * mm, "end": v(105, -14.88) * mm});
            skLineSegment(sketch, "E235", {"start": v(110.25, 0) * mm, "end": v(113.75, 0) * mm});
            skLineSegment(sketch, "E236", {"start": v(110.25, -28) * mm, "end": v(113.75, -28) * mm});
            skLineSegment(sketch, "E237", {"start": v(40.25, -17.5) * mm, "end": v(45.5, -14.88) * mm});
            skLineSegment(sketch, "E238", {"start": v(45.5, -13.13) * mm, "end": v(40.25, -10.5) * mm});
            skLineSegment(sketch, "E239", {"start": v(110.25, -10.5) * mm, "end": v(105, -13.13) * mm});
            skLineSegment(sketch, "E240", {"start": v(110.25, -17.5) * mm, "end": v(105, -14.88) * mm});
            skFitSpline(sketch, "E241", {"points": [v(40.25, -21) * mm, v(57.75, -24.5) * mm, v(75.25, -28) * mm], "startDerivative": vector(52.5, 0) * mm, "endDerivative": vector(52.5, 0) * mm});
            skFitSpline(sketch, "E242", {"points": [v(40.25, -22.75) * mm, v(57.75, -26.25) * mm, v(75.25, -29.75) * mm], "startDerivative": vector(52.5, 0) * mm, "endDerivative": vector(52.5, 0) * mm});
            skFitSpline(sketch, "E243", {"points": [v(40.25, -26.25) * mm, v(57.75, -29.75) * mm, v(75.25, -33.25) * mm], "startDerivative": vector(52.5, 0) * mm, "endDerivative": vector(52.5, 0) * mm});
            skFitSpline(sketch, "E244", {"points": [v(40.25, -28) * mm, v(57.75, -31.5) * mm, v(75.25, -35) * mm], "startDerivative": vector(52.5, 0) * mm, "endDerivative": vector(52.5, 0) * mm});
            skFitSpline(sketch, "E245", {"points": [v(110.25, -1.75) * mm, v(92.75, 1.75) * mm, v(75.25, 5.25) * mm], "startDerivative": vector(-52.5, 0) * mm, "endDerivative": vector(-52.5, 0) * mm});
            skFitSpline(sketch, "E246", {"points": [v(110.25, 0) * mm, v(92.75, 3.5) * mm, v(75.25, 7) * mm], "startDerivative": vector(-52.5, 0) * mm, "endDerivative": vector(-52.5, 0) * mm});
            skFitSpline(sketch, "E247", {"points": [v(75.25, 1.75) * mm, v(92.75, -1.75) * mm, v(110.25, -5.25) * mm], "startDerivative": vector(52.5, 0) * mm, "endDerivative": vector(52.5, 0) * mm});
            skFitSpline(sketch, "E248", {"points": [v(75.25, 0) * mm, v(92.75, -3.5) * mm, v(110.24, -6.97) * mm], "startDerivative": vector(52.5, 0) * mm, "endDerivative": vector(52.5, 0) * mm});
            skFitSpline(sketch, "E249", {"points": [v(75.25, -35) * mm, v(92.75, -31.5) * mm, v(110.25, -28) * mm], "startDerivative": vector(52.5, 0) * mm, "endDerivative": vector(52.5, 0) * mm});
            skFitSpline(sketch, "E250", {"points": [v(75.25, -33.25) * mm, v(92.75, -29.75) * mm, v(110.25, -26.25) * mm], "startDerivative": vector(52.5, 0) * mm, "endDerivative": vector(52.5, 0) * mm});
            skFitSpline(sketch, "E251", {"points": [v(75.25, -29.75) * mm, v(92.75, -26.25) * mm, v(110.25, -22.75) * mm], "startDerivative": vector(52.5, 0) * mm, "endDerivative": vector(52.5, 0) * mm});
            skFitSpline(sketch, "E252", {"points": [v(75.25, -27.97) * mm, v(92.75, -24.47) * mm, v(110.25, -20.97) * mm], "startDerivative": vector(52.5, 0) * mm, "endDerivative": vector(52.5, 0) * mm});
            skLineSegment(sketch, "E253", {"start": v(73.5, 3.53) * mm, "end": v(73.5, 5.23) * mm});
            skLineSegment(sketch, "E254", {"start": v(73.5, 5.23) * mm, "end": v(73.5, 1.73) * mm});
            skLineSegment(sketch, "E255", {"start": v(77, 3.53) * mm, "end": v(77, 5.23) * mm});
            skLineSegment(sketch, "E256", {"start": v(77, 5.23) * mm, "end": v(77, 1.73) * mm});
            skLineSegment(sketch, "E257", {"start": v(73.5, -31.53) * mm, "end": v(73.5, -29.73) * mm});
            skLineSegment(sketch, "E258", {"start": v(73.5, -29.73) * mm, "end": v(73.5, -33.23) * mm});
            skLineSegment(sketch, "E259", {"start": v(77, -29.73) * mm, "end": v(77, -33.23) * mm});
            skLineSegment(sketch, "E260.trimOffspring", {"start": v(40.25, -22.75) * mm, "end": v(40.25, -26.25) * mm});
            skLineSegment(sketch, "E261.trimOffspring", {"start": v(40.25, -17.5) * mm, "end": v(40.25, -21) * mm});
            skLineSegment(sketch, "E262.trimOffspring", {"start": v(40.25, -7) * mm, "end": v(40.25, -10.5) * mm});
            skLineSegment(sketch, "E263.trimOffspring", {"start": v(110.25, -21) * mm, "end": v(110.25, -17.5) * mm});
            skLineSegment(sketch, "E264.trimOffspring", {"start": v(110.25, -10.5) * mm, "end": v(110.25, -7) * mm});
            skLineSegment(sketch, "E265.trimOffspring", {"start": v(110.25, -5.25) * mm, "end": v(110.25, -1.75) * mm});
            skLineSegment(sketch, "E266.left", {"start": v(113.75, -28) * mm, "end": v(113.75, 0) * mm});
            skPoint(sketch, "E267", {"position": v(36.75, 0) * mm});
            skLineSegment(sketch, "E268", {"start": v(40.25, -28) * mm, "end": v(36.75, -28) * mm});
            skLineSegment(sketch, "E269", {"start": v(36.75, -1.73) * mm, "end": v(36.75, -5.25) * mm});
            skLineSegment(sketch, "E270", {"start": v(38.5, 0) * mm, "end": v(36.75, 0) * mm});
            skPoint(sketch, "E271.startDerivative.orphan", {"position": v(66.5, 7) * mm});
            skPoint(sketch, "E272.start.orphan", {"position": v(40.25, -5.25) * mm});
            skPoint(sketch, "E272.startDerivative.orphan", {"position": v(49, -5.25) * mm});
            skPoint(sketch, "E273.start.orphan", {"position": v(40.25, -7) * mm});
            skPoint(sketch, "E273.startDerivative.orphan", {"position": v(49, -7) * mm});
            skPoint(sketch, "E274.start.orphan", {"position": v(40.25, -1.75) * mm});
            skPoint(sketch, "E274.startDerivative.orphan", {"position": v(49, -1.75) * mm});
            skLineSegment(sketch, "E275.trimOffspring", {"start": v(36.75, -17.5) * mm, "end": v(36.75, -20.97) * mm});
            skLineSegment(sketch, "E276.trimOffspring", {"start": v(40.25, -10.5) * mm, "end": v(40.25, -6.98) * mm});
            skLineSegment(sketch, "E277.trimOffspring", {"start": v(36.75, -6.98) * mm, "end": v(36.75, -10.5) * mm});
            skLineSegment(sketch, "E278.trimOffspring", {"start": v(36.75, -22.75) * mm, "end": v(36.75, -26.25) * mm});
            skLineSegment(sketch, "E279.trimOffspring", {"start": v(40.25, -6.98) * mm, "end": v(40.25, -10.5) * mm});
            skLineSegment(sketch, "E280.trimOffspring", {"start": v(40.25, -5.25) * mm, "end": v(40.25, -1.73) * mm});
            skPoint(sketch, "E281.startDerivative.orphan", {"position": v(10.5, 26.25) * mm});
            skPoint(sketch, "E282.startDerivative.orphan", {"position": v(10.5, 22.75) * mm});
            skLineSegment(sketch, "E283.trimOffspring", {"start": v(0, 21.02) * mm, "end": v(0, 6.98) * mm});
            skLineSegment(sketch, "E284.trimOffspring", {"start": v(40.25, 34.98) * mm, "end": v(40.25, 38.5) * mm});
            skLineSegment(sketch, "E285.trimOffspring", {"start": v(36.75, 38.5) * mm, "end": v(36.75, 34.98) * mm});
            skLineSegment(sketch, "E286.trimOffspring", {"start": v(40.25, 45.5) * mm, "end": v(40.25, 48.97) * mm});
            skLineSegment(sketch, "E287.trimOffspring", {"start": v(36.75, 34.98) * mm, "end": v(36.75, 38.5) * mm});
            skPoint(sketch, "E288.startDerivative.orphan", {"position": v(66.5, 5.25) * mm});
            skPoint(sketch, "E289.startDerivative.orphan", {"position": v(66.5, 1.75) * mm});
            skLineSegment(sketch, "E290.trimOffspring", {"start": v(40.25, 50.75) * mm, "end": v(40.25, 54.25) * mm});
            skSolve(sketch);
        }
        {
            var Q0;
            Q0 = qSketchRegion(id + "F0", true);
            extrude(context, id + "F1", {"entities" : qUnion([Q0]), "depth" : 25 * mm, "offsetDistance" : 25 * mm});
        }
    });
